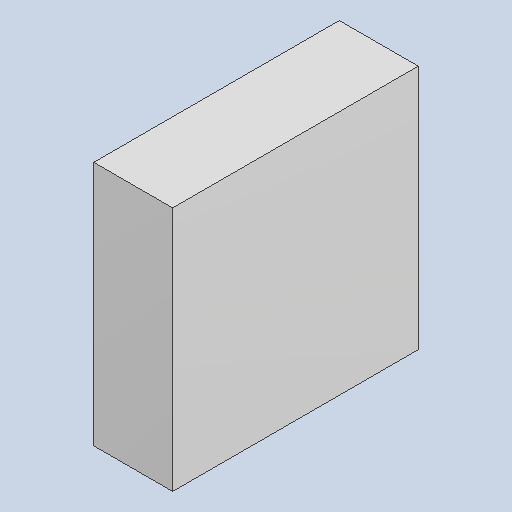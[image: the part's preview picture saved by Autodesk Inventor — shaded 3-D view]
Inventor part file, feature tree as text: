
AUTODESK INVENTOR PART (.ipt)
format: ipt  version: 2023.4 (Build 274418000, 418)  size: 81,408 bytes
history: native  units: mm
features: extrude x1
ambient origin geometry x8: Origin, YZ Plane, XZ Plane, XY Plane, X Axis, Y Axis, Z Axis, Center Point
bodies: Solid1 (feature_tree)
feature tree (1):
  extrude  "Extruded_5"  [1 undecoded]
note: 1 required parameter value undecoded (feature->parameter linkage not recoverable at this tier; creation-order binding heuristic only, values carry confidence <= 0.55)
